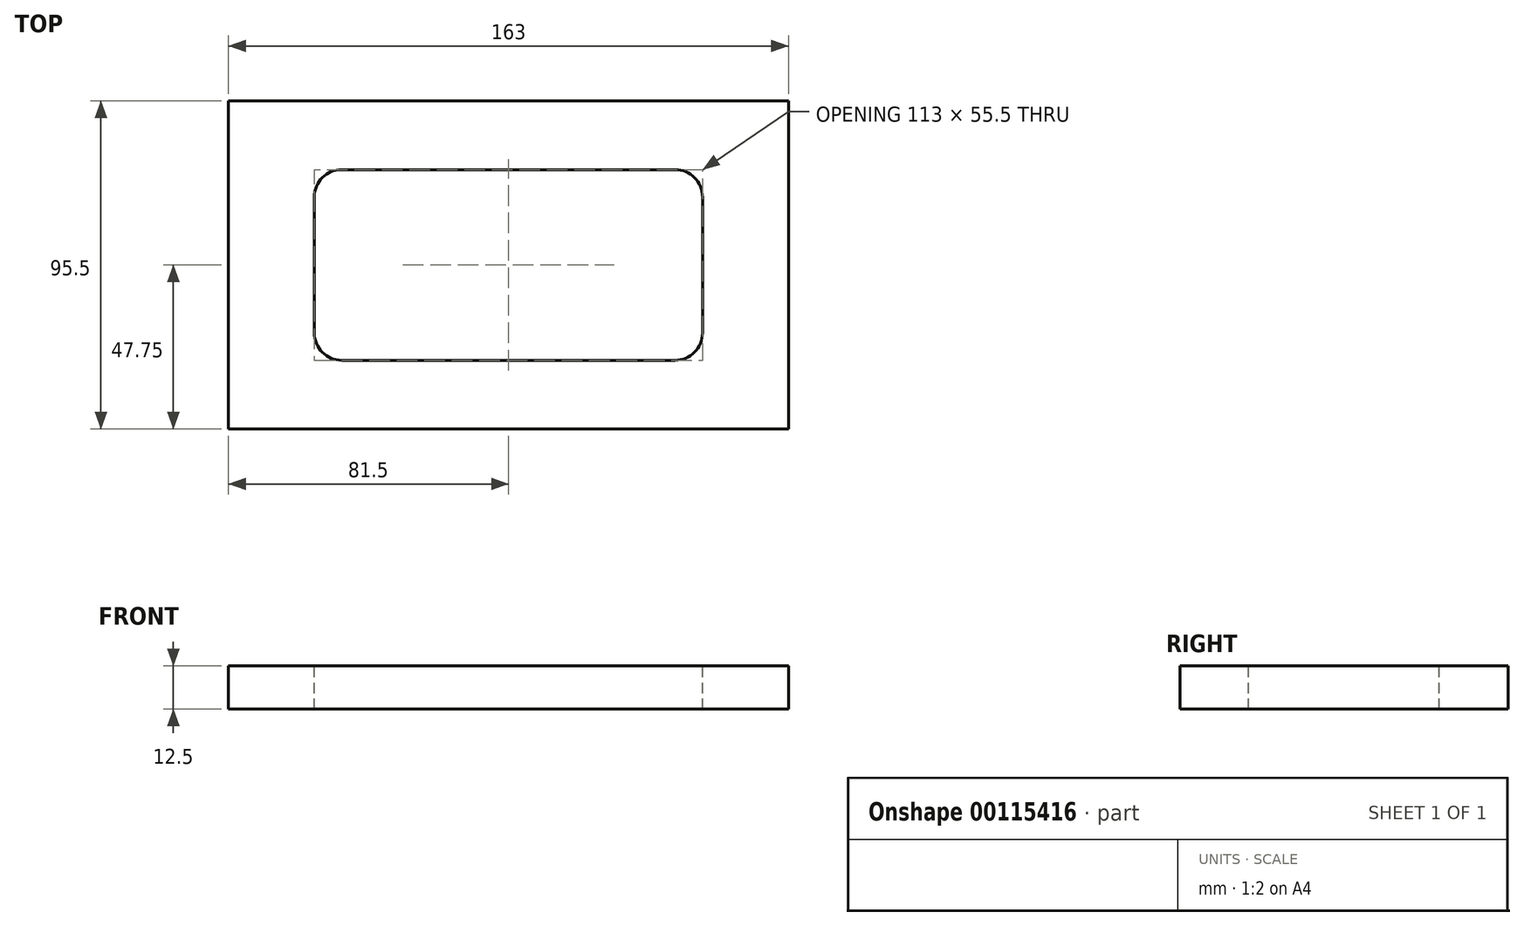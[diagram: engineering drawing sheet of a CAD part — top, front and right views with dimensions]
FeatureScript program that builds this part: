
annotation { "Feature Type Name" : "Feature", "Feature Type Description" : "" }
export const myFeature = defineFeature(function(context is Context, id is Id, definition is map)
    precondition{}
    {
        {
            assignVariable(context, id + "F0", {"name" : "depth", "anyValue" : 12.5});
        }
        {
            var Q0;
            Q0=qCreatedBy(makeId("Top.planeOp"),FACE);
            var sketch = newSketch(context, id + "F1", { "sketchPlane" : qUnion([Q0])});
            skArc(sketch, "E0", {"start": v(-48.5, 27.75) * mm, "mid": v(-54.16, 25.4) * mm, "end": v(-56.5, 19.75) * mm});
            skArc(sketch, "E1", {"start": v(-56.5, -19.75) * mm, "mid": v(-54.16, -25.4) * mm, "end": v(-48.5, -27.75) * mm});
            skArc(sketch, "E2", {"start": v(56.5, 19.75) * mm, "mid": v(54.16, 25.4) * mm, "end": v(48.5, 27.75) * mm});
            skArc(sketch, "E3", {"start": v(48.5, -27.75) * mm, "mid": v(54.16, -25.4) * mm, "end": v(56.5, -19.75) * mm});
            skLineSegment(sketch, "E4", {"start": v(-48.5, 27.75) * mm, "end": v(48.5, 27.75) * mm});
            skLineSegment(sketch, "E5", {"start": v(56.5, 19.75) * mm, "end": v(56.5, -19.75) * mm});
            skLineSegment(sketch, "E6", {"start": v(-48.5, -27.75) * mm, "end": v(48.5, -27.75) * mm});
            skLineSegment(sketch, "E7", {"start": v(-56.5, 19.75) * mm, "end": v(-56.5, -19.75) * mm});
            skLineSegment(sketch, "E8.bottom", {"start": v(-81.5, 47.75) * mm, "end": v(81.5, 47.75) * mm});
            skLineSegment(sketch, "E8.top", {"start": v(-81.5, -47.75) * mm, "end": v(81.5, -47.75) * mm});
            skLineSegment(sketch, "E8.left", {"start": v(-81.5, 47.75) * mm, "end": v(-81.5, -47.75) * mm});
            skLineSegment(sketch, "E8.right", {"start": v(81.5, 47.75) * mm, "end": v(81.5, -47.75) * mm});
            skSolve(sketch);
        }
        {
            var Q0;
            Q0=makeQuery(id+"F1.imprint","IMPRINT",FACE,{"disambiguationData":[TD([[makeQuery(id+"F1.imprint","IMPRINT",EDGE,{"derivedFrom":sQuery(id+"F1.wireOp",EDGE,"E0")}),-1.0]])]});
            extrude(context, id + "F2", {"entities" : qUnion([Q0]), "oppositeDirection" : true, "depth" : (getVariable(context, 'depth')) * mm});
        }
    });
